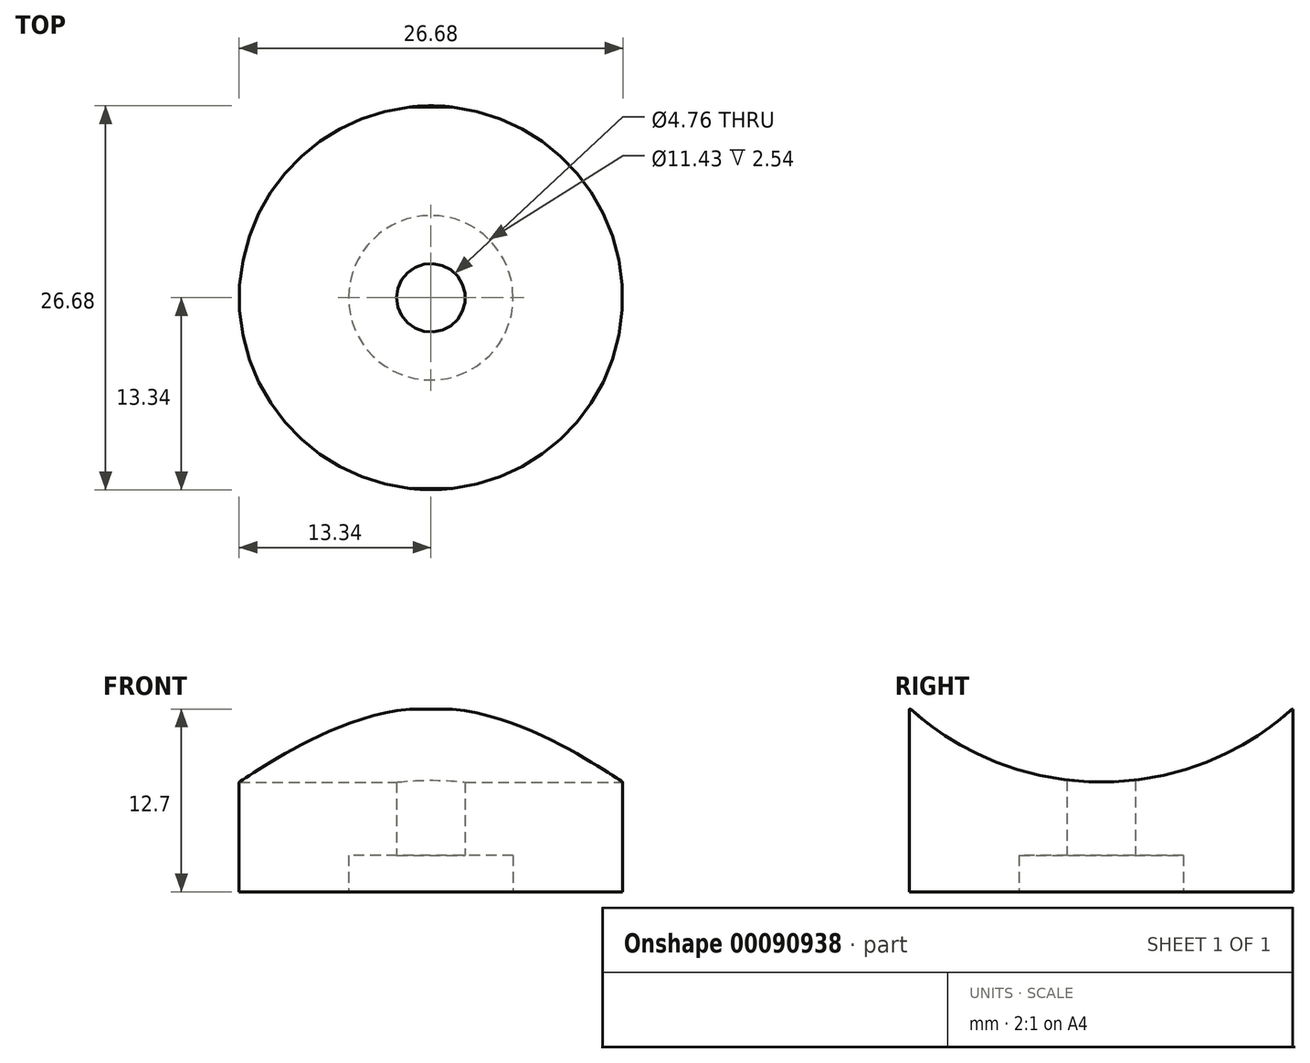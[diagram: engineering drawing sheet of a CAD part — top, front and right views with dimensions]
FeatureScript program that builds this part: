
annotation { "Feature Type Name" : "Feature", "Feature Type Description" : "" }
export const myFeature = defineFeature(function(context is Context, id is Id, definition is map)
    precondition{}
    {
        {
            var Q0;
            Q0=qCreatedBy(makeId("Top.planeOp"),FACE);
            var sketch = newSketch(context, id + "F0", { "sketchPlane" : qUnion([Q0])});
            skCircle(sketch, "E0", {"center": v(0, 0) * mm, "radius": 2.38 * mm});
            skCircle(sketch, "E1", {"center": v(0, 0) * mm, "radius": 5.72 * mm});
            skCircle(sketch, "E2", {"center": v(0, 0) * mm, "radius": 13.34 * mm});
            skSolve(sketch);
        }
        {
            var Q0;
            Q0=makeQuery(id+"F0.imprint","IMPRINT",FACE,{"disambiguationData":[TD([[makeQuery(id+"F0.imprint","IMPRINT",EDGE,{"derivedFrom":sQuery(id+"F0.wireOp",EDGE,"E0")}),-1.0]])]});
            var Q1;
            Q1=makeQuery(id+"F0.imprint","IMPRINT",FACE,{"disambiguationData":[TD([[makeQuery(id+"F0.imprint","IMPRINT",EDGE,{"derivedFrom":sQuery(id+"F0.wireOp",EDGE,"E1")}),-1.0]])]});
            extrude(context, id + "F1", {"entities" : qUnion([Q0, Q1]), "depth" : 12.7 * mm});
        }
        {
            var Q0;
            Q0=makeQuery(id+"F0.imprint","IMPRINT",FACE,{"disambiguationData":[TD([[makeQuery(id+"F0.imprint","IMPRINT",EDGE,{"derivedFrom":sQuery(id+"F0.wireOp",EDGE,"E0")}),-1.0]])]});
            extrude(context, id + "F2", {"entities" : qUnion([Q0]), "operationType" : NewBodyOperationType.REMOVE, "depth" : 2.54 * mm});
        }
        {
            var Q0;
            Q0=qCreatedBy(makeId("Right.planeOp"),FACE);
            var sketch = newSketch(context, id + "F3", { "sketchPlane" : qUnion([Q0])});
            skCircle(sketch, "E3", {"center": v(0, 27.45) * mm, "radius": 19.83 * mm});
            skSolve(sketch);
        }
        {
            var Q0;
            Q0=makeQuery(id+"F3.imprint","IMPRINT",FACE,{"disambiguationData":[TD([[makeQuery(id+"F3.imprint","IMPRINT",EDGE,{"derivedFrom":sQuery(id+"F3.wireOp",EDGE,"E3")}),1.0]])]});
            extrude(context, id + "F4", {"entities" : qUnion([Q0]), "operationType" : NewBodyOperationType.REMOVE, "endBound" : BoundingType.THROUGH_ALL, "oppositeDirection" : true, "depth" : 25.4 * mm, "hasSecondDirection" : true, "secondDirectionBound" : SecondDirectionBoundingType.THROUGH_ALL, "secondDirectionOppositeDirection" : false, "secondDirectionDepth" : 25.4 * mm});
        }
    });
